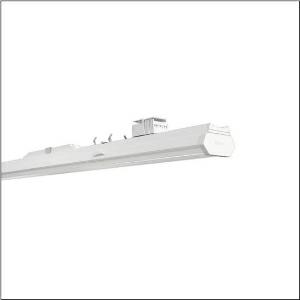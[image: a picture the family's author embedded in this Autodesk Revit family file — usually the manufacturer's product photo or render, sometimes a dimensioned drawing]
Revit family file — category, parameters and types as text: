
# Revit family: licross_r__11_protected_ho_51td1bdn4e5m3c_9259
name_source: partatom
category: Lighting Fixtures
units: mm (PartAtom-declared; Revit-internal decimal feet)

## family parameters
Cut with Voids When Loaded = No
Host = Face
Light Source = No
Part Type = Normal
Room Calculation Point = No
Round Connector Dimension = Use Diameter
Shared = No

## types (1)
- --- (1 x LED, 920 lm, 7.4 W, 4000K)
    Apparent Load = 7 VA
    CIE Flux Codes = 54 82 95 97 100
    Color Rendering = 80
    Color Temperature = 4000K
    Default Elevation = 1800 mm
    Description = Licross® 11 Protected HO, luminaire insert, of sheet steel, galvanised, coil coated, white, length: 1.500mm, width: 90mm, height: 101mm, LED rated luminous flux: 14.500lm, light colour: 840, control gear: DALI 2 (for two DALI lines), with plug, 6-pole, with phase selection, for trunking rail, 14-core, mains connection: 220..240V, AC, 50/60Hz, rated input power: 91W, for trunking rail, 14-core, internal wiring halogen-free, for emergency light function, converter,control gear: single battery element, battery: LiFePO4, 9Ah, primary optical cover: cover, of PMMA, light emission: direct distribution, primary light characteristic: symmetric, protection rating (complete): IP54, insulation class (complete): insulation class I (protective earthing), certification: CE, UKCA, protection symbol: D if used in an environment with non-conductive dust loads with corresponding accessories, impact resistance: IK06, permissible ambient temperature for indoor applications: +5..+30°C, standard: EN 60598-2-22, LABS conformity tested according to VDMA 24364:2018-05, reducing of maximum allowable ambient temperature of 5°C with ceiling mounting, corresponds to IFS (International Featured Standards) requirements for safety and quality in the food industry, packaging unit: 1 piece
    Height = 92 mm
    Lamp = 1 x LED
    Lamp Light Flux = 920 lm
    Lamp Power = 7.4 W
    Lamp count = 1
    Length = 1500 mm
    Luminous efficacy = 124 lm/W
    Manufacturer = Siteco
    ModVariant = No
    Model = 51TD1BDN4E5M3C
    Mounting Place = Ceiling
    Mounting Type = Pendant
    Number of Poles = 1
    OnlyDefault = Yes
    Power Factor = 1
    Product Name = Licross® 11 Protected HO
    Product group = luminaire insert | ceiling pendant
    ProductGroupID = 902
    Protection Class = Protection class I
    Protection Degree = IP 54
    RLX_Detail_Level = 1
    RLX_Emergency_Light_Flux = 0 lm
    RLX_Emergency_Type = 0
    RLX_Emergency_Type_DB = No
    RlxData = <blob elided: 24801 chars, md5=46c62bc0>
    Socket = socket
    Standby Power = 0 W
    System Light Flux = 920 lm
    System Power = 7 W
    Type Comments = : emergency light operation: 3 h
    Type Image = l_1256145.jpg
    URL = http://relux.com
    VarID = @adj_112805
    Voltage = 0 V
    Weight = 0.00 kg
    Width = 88 mm

## geometry (parser evidence)
native form markers: Blend x4, Sweep x12
no freeform markers — native parametric forms only
